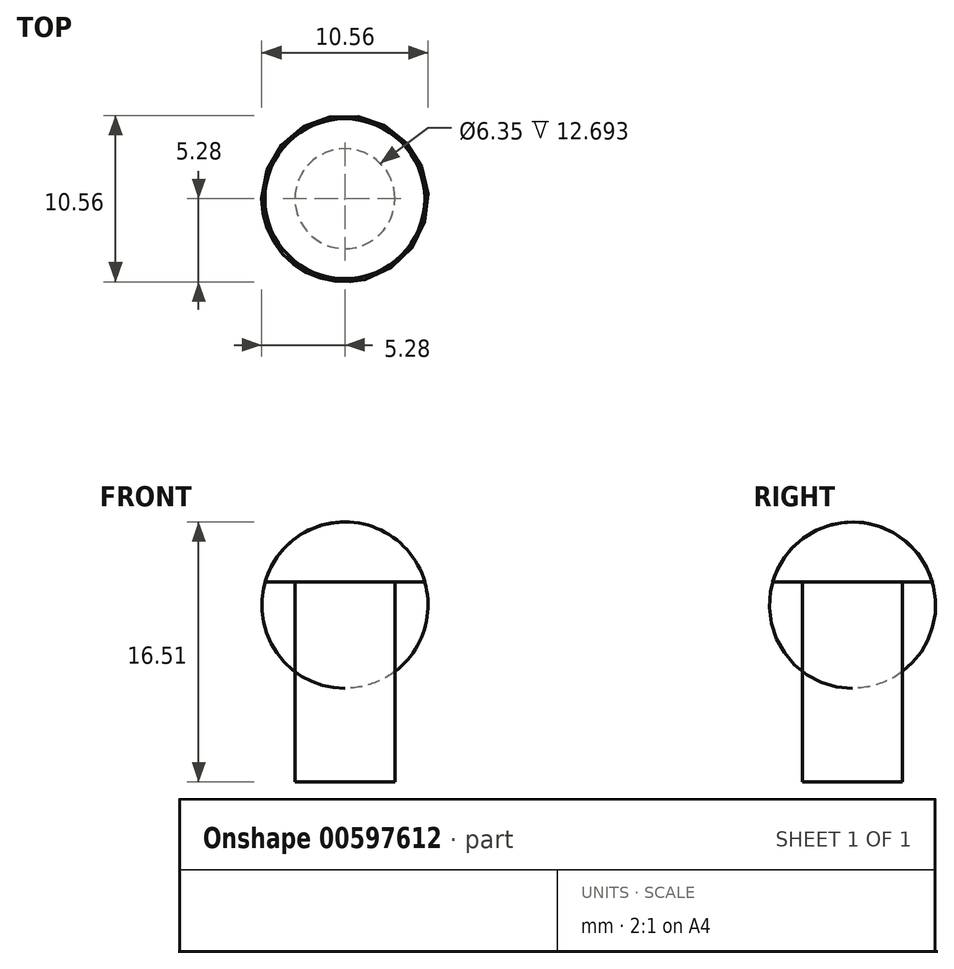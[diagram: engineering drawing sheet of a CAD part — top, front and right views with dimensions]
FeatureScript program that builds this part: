
annotation { "Feature Type Name" : "Feature", "Feature Type Description" : "" }
export const myFeature = defineFeature(function(context is Context, id is Id, definition is map)
    precondition{}
    {
        {
            var Q0;
            Q0=qCreatedBy(makeId("Front.planeOp"),FACE);
            var sketch = newSketch(context, id + "F0", { "sketchPlane" : qUnion([Q0])});
            skLineSegment(sketch, "E0", {"start": v(0, 0) * mm, "end": v(0, 16.5) * mm});
            skLineSegment(sketch, "E1", {"start": v(0, 16.5) * mm, "end": v(0, 0) * mm});
            skLineSegment(sketch, "E2", {"start": v(0, 0) * mm, "end": v(3.17, 0) * mm});
            skLineSegment(sketch, "E3", {"start": v(3.17, 0) * mm, "end": v(3.17, 12.7) * mm});
            skLineSegment(sketch, "E4", {"start": v(0, 12.7) * mm, "end": v(5.08, 12.7) * mm});
            skArc(sketch, "E5", {"start": v(5.08, 12.7) * mm, "mid": v(3.18, 15.45) * mm, "end": v(0, 16.51) * mm});
            skSolve(sketch);
        }
        {
            var Q0;
            Q0=qSketchRegion(id+"F0",true);
            var Q1;
            Q1=sQuery(id+"F0.wireOp",EDGE,"E1");
            revolve(context, id + "F1", {"entities" : qUnion([Q0]), "axis" : qUnion([Q1]), "revolveType" : RevolveType.FULL});
        }
    });
